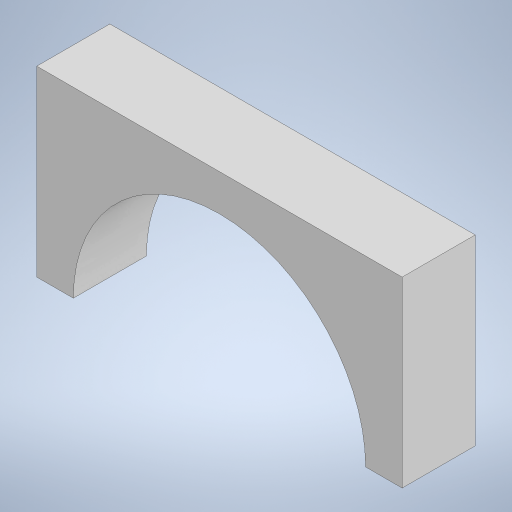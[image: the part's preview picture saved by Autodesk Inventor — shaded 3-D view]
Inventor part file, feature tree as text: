
AUTODESK INVENTOR PART (.ipt)
format: ipt  version: 2023 (Build 270158000, 158)  size: 211,456 bytes
history: native  units: mm
features: extrude x2, sketch x2
ambient origin geometry x8: Origin, YZ Plane, XZ Plane, XY Plane, X Axis, Y Axis, Z Axis, Center Point
bodies: Body1 (feature_tree)
feature tree (4):
  extrude  "Extrusion11"  Depth=50.0mm
  extrude  "Extrusion12"  Depth=20.0mm
  sketch  "Sketch13"  dims[d42=100.0mm d43=50.0mm]
  sketch  "Sketch14"  dims[d44=20.0mm d45=0.0mm d46=80.0mm d47=20.0mm d48=0.0mm]
